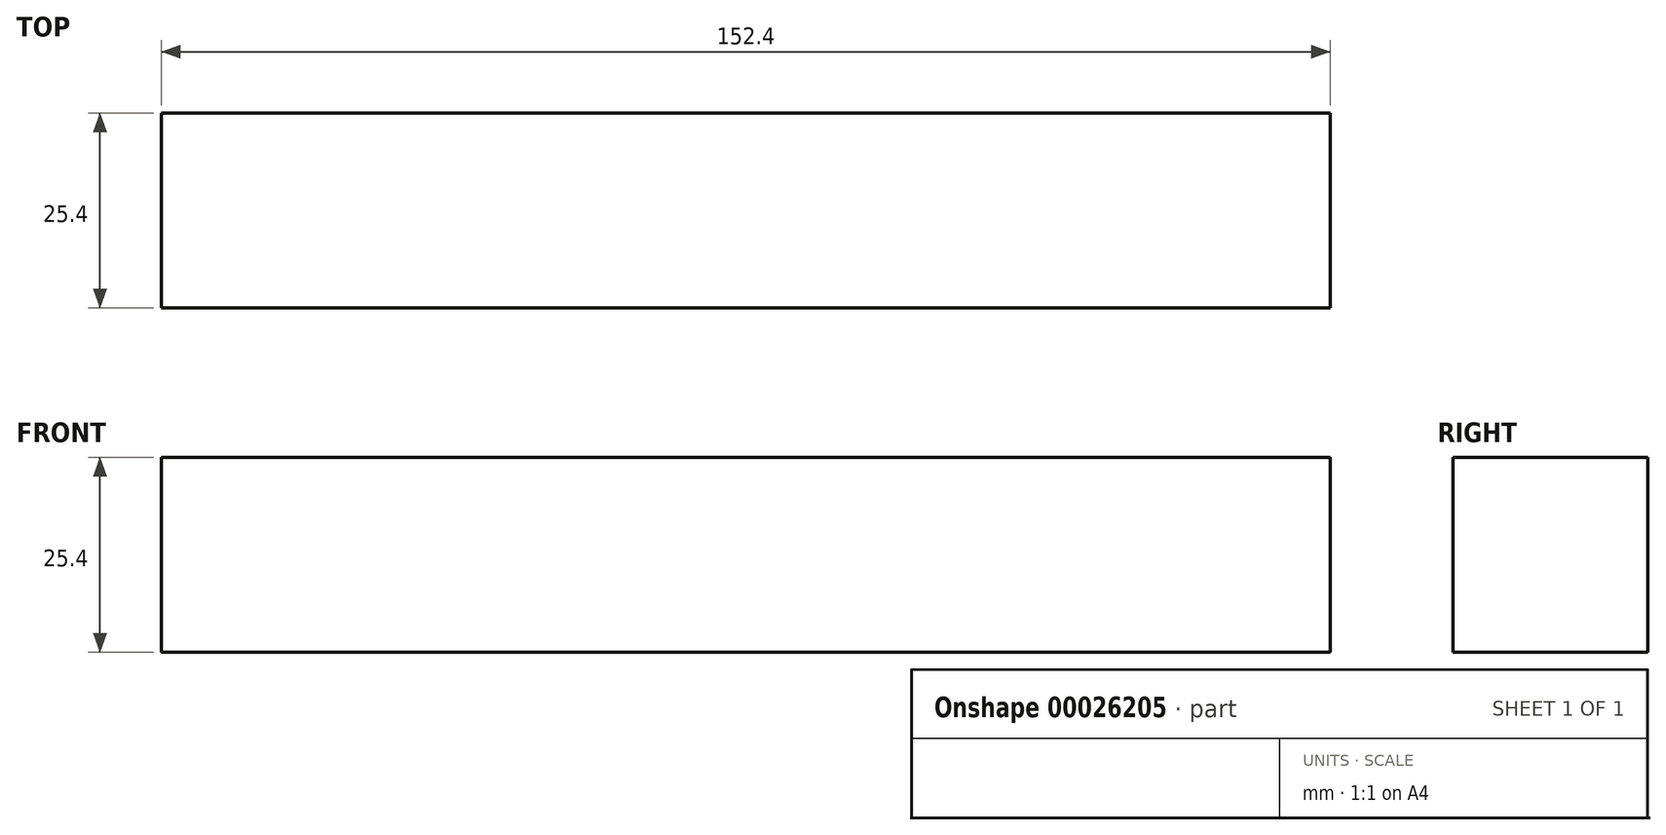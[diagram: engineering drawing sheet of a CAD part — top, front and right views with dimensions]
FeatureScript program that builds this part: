
annotation { "Feature Type Name" : "Feature", "Feature Type Description" : "" }
export const myFeature = defineFeature(function(context is Context, id is Id, definition is map)
    precondition{}
    {
        {
            var Q0;
            Q0=qCreatedBy(makeId("Front.planeOp"),FACE);
            var sketch = newSketch(context, id + "F0", { "sketchPlane" : qUnion([Q0])});
            skLineSegment(sketch, "E0.bottom", {"start": v(-63.71, 26.82) * mm, "end": v(88.69, 26.82) * mm});
            skLineSegment(sketch, "E0.top", {"start": v(-63.71, 1.42) * mm, "end": v(88.69, 1.42) * mm});
            skLineSegment(sketch, "E0.left", {"start": v(-63.71, 26.82) * mm, "end": v(-63.71, 1.42) * mm});
            skLineSegment(sketch, "E0.right", {"start": v(88.69, 26.82) * mm, "end": v(88.69, 1.42) * mm});
            skSolve(sketch);
        }
        {
            var Q0;
            Q0=makeQuery(id+"F0.imprint","IMPRINT",FACE,{"disambiguationData":[TD([[makeQuery(id+"F0.imprint","IMPRINT",EDGE,{"derivedFrom":sQuery(id+"F0.wireOp",EDGE,"E0.bottom")}),-1.0]])]});
            extrude(context, id + "F1", {"entities" : qUnion([Q0]), "depth" : 25.4 * mm});
        }
    });
